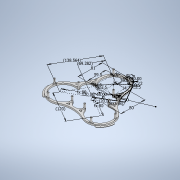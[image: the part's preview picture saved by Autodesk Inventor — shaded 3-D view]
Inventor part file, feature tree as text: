
AUTODESK INVENTOR PART (.ipt)
format: ipt  version: 2021 (Build 250183000, 183)  size: 547,840 bytes
history: native  units: mm
features: extrude x4, mirror x2, pattern_circular x2, fillet x1
ambient origin geometry x8: Origin, YZ Plane, XZ Plane, XY Plane, X Axis, Y Axis, Z Axis, Center Point
bodies: Solid1 (feature_tree), Body (feature_tree), Solid2 (feature_tree)
feature tree (9):
  extrude  "Extrusion1"  Depth=59.5mm
  extrude  "Extrusion2"  Depth=59.5mm
  fillet  "Fillet1"  Radius=2.5mm
  mirror  "Mirror1"
  pattern_circular  "Circular Pattern1"  [2 undecoded]
  extrude  "Extrusion3"  Depth=6.0mm
  extrude  "Extrusion4"  Depth=6.0mm
  mirror  "Mirror2"
  pattern_circular  "Circular Pattern2"  [2 undecoded]
note: 4 required parameter values undecoded (feature->parameter linkage not recoverable at this tier; creation-order binding heuristic only, values carry confidence <= 0.55)
